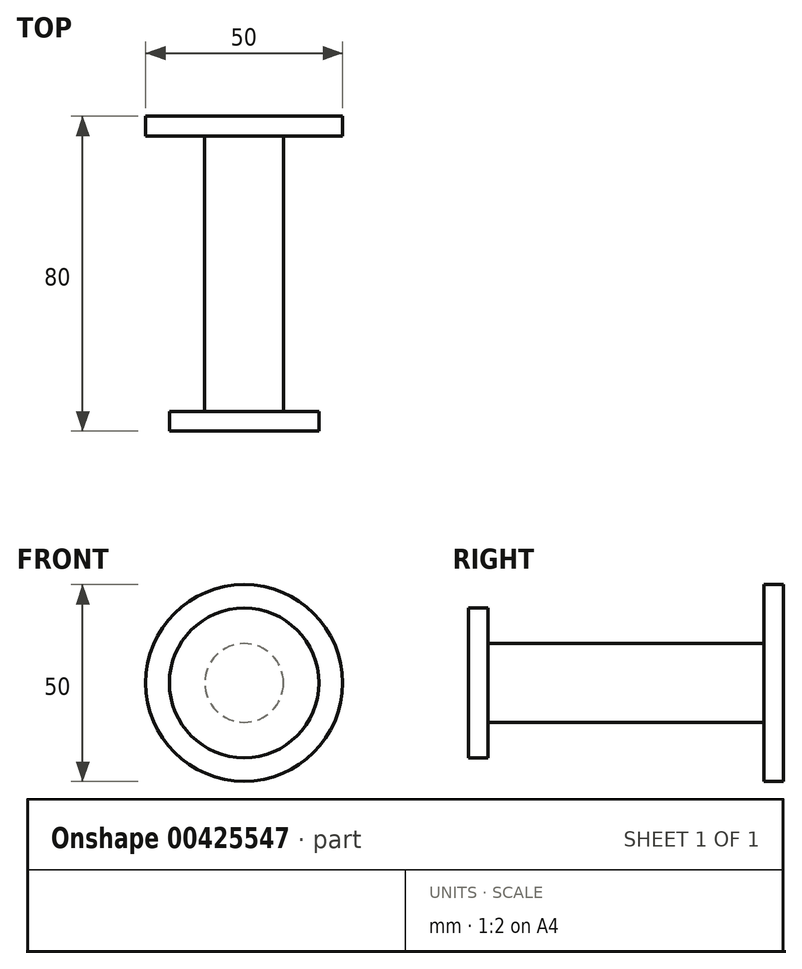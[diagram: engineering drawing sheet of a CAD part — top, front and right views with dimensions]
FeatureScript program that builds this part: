
annotation { "Feature Type Name" : "Feature", "Feature Type Description" : "" }
export const myFeature = defineFeature(function(context is Context, id is Id, definition is map)
    precondition{}
    {
        {
            var Q0;
            Q0=qCreatedBy(makeId("Front.planeOp"),FACE);
            var sketch = newSketch(context, id + "F0", { "sketchPlane" : qUnion([Q0])});
            skCircle(sketch, "E0", {"center": v(0, 0) * mm, "radius": 25 * mm});
            skSolve(sketch);
        }
        {
            var Q0;
            Q0 = qSketchRegion(id + "F0", true);
            var Q1;
            Q1=makeQuery(id+"F0.imprint","IMPRINT",FACE,{"disambiguationData":[TD([[makeQuery(id+"F0.imprint","IMPRINT",EDGE,{"derivedFrom":sQuery(id+"F0.wireOp",EDGE,"E0")}),1.0]])]});
            extrude(context, id + "F1", {"entities" : qUnion([Q0, Q1]), "depth" : 5 * mm});
        }
        {
            var Q0;
            Q0=makeQuery(id+"F1.opExtrude","CAP_FACE",FACE,{"disambiguationData":[OSD([sQuery(id+"F0.wireOp",EDGE,"E0")])],"isStart":false});
            var sketch = newSketch(context, id + "F2", { "sketchPlane" : qUnion([Q0])});
            skCircle(sketch, "E1", {"center": v(0, 0) * mm, "radius": 10 * mm});
            skSolve(sketch);
        }
        {
            var Q0;
            Q0=makeQuery(id+"F2.imprint","IMPRINT",FACE,{"disambiguationData":[TD([[makeQuery(id+"F2.imprint","IMPRINT",EDGE,{"derivedFrom":sQuery(id+"F2.wireOp",EDGE,"E1")}),1.0]])]});
            extrude(context, id + "F3", {"entities" : qUnion([Q0]), "operationType" : NewBodyOperationType.ADD, "depth" : 70 * mm});
        }
        {
            var Q0;
            Q0=makeQuery(id+"F3.opExtrude","CAP_FACE",FACE,{"disambiguationData":[OSD([sQuery(id+"F2.wireOp",EDGE,"E1")])],"isStart":false});
            var sketch = newSketch(context, id + "F4", { "sketchPlane" : qUnion([Q0])});
            skCircle(sketch, "E2", {"center": v(0, 0) * mm, "radius": 19 * mm});
            skSolve(sketch);
        }
        {
            var Q0;
            Q0 = qSketchRegion(id + "F4", true);
            extrude(context, id + "F5", {"entities" : qUnion([Q0]), "operationType" : NewBodyOperationType.ADD, "depth" : 5 * mm});
        }
    });
